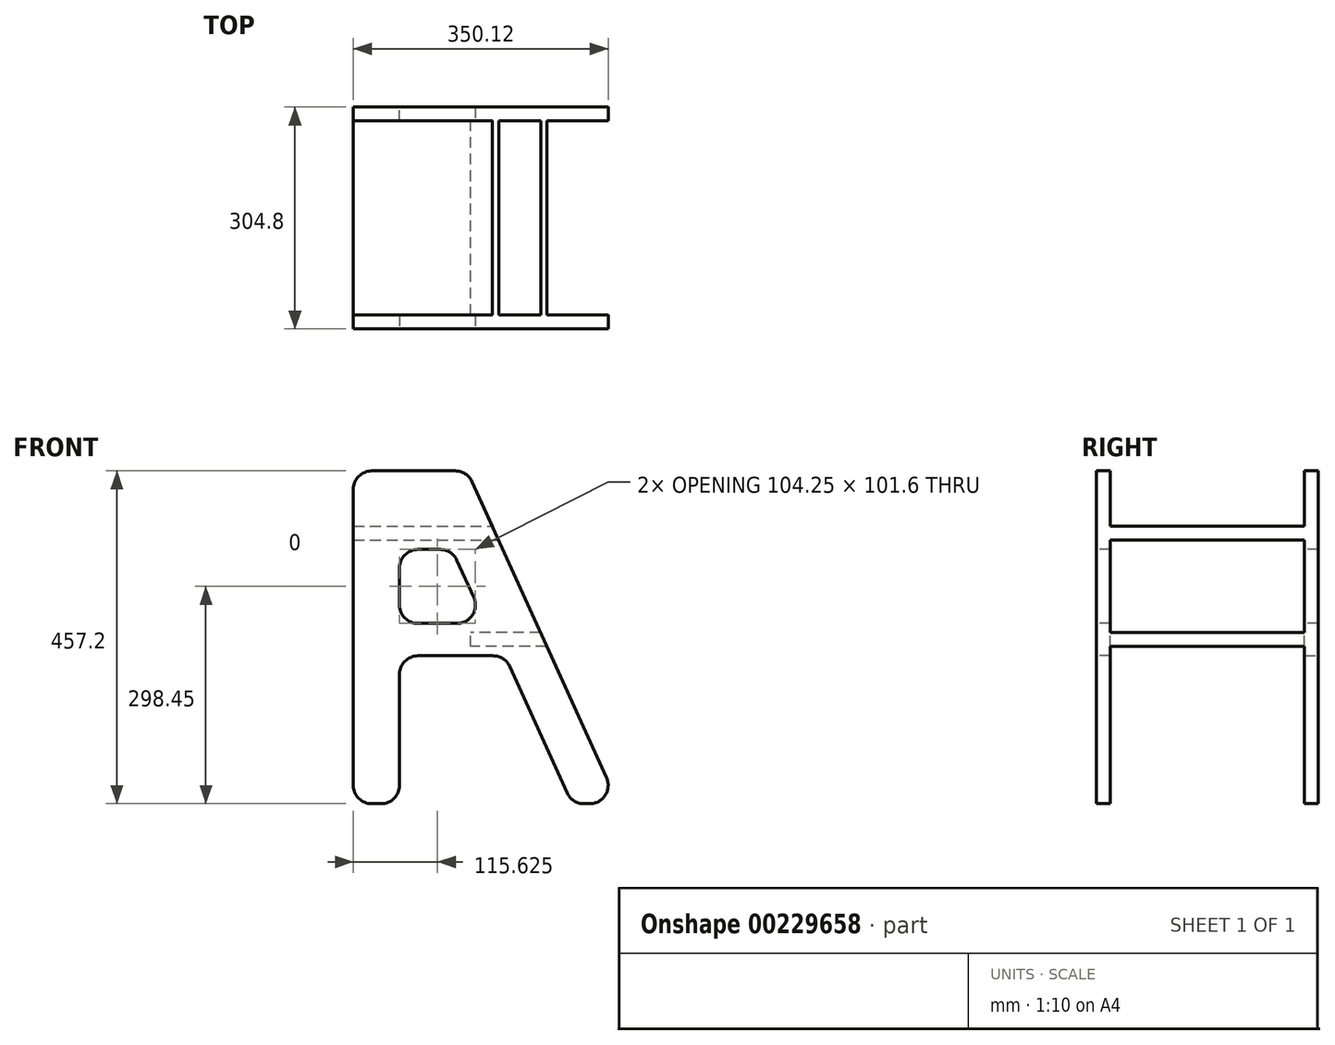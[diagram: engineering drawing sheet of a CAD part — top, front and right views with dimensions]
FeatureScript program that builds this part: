
annotation { "Feature Type Name" : "Feature", "Feature Type Description" : "" }
export const myFeature = defineFeature(function(context is Context, id is Id, definition is map)
    precondition{}
    {
        {
            var Q0;
            Q0=qCreatedBy(makeId("Front.planeOp"),FACE);
            var sketch = newSketch(context, id + "F0", { "sketchPlane" : qUnion([Q0])});
            skLineSegment(sketch, "E0", {"start": v(156.34, 0) * mm, "end": v(153.47, 0) * mm});
            skLineSegment(sketch, "E1", {"start": v(-140.3, 0) * mm, "end": v(-127.6, 0) * mm});
            skLineSegment(sketch, "E2", {"start": v(-165.7, 25.4) * mm, "end": v(-165.7, 304.8) * mm});
            skLineSegment(sketch, "E3", {"start": v(-140.3, 330.2) * mm, "end": v(-25.68, 330.2) * mm});
            skLineSegment(sketch, "E4", {"start": v(-4.4, 318.66) * mm, "end": v(177.62, 39.26) * mm});
            skLineSegment(sketch, "E5", {"start": v(132.19, 11.54) * mm, "end": v(51.03, 136.1) * mm});
            skLineSegment(sketch, "E6", {"start": v(29.75, 147.64) * mm, "end": v(-76.8, 147.64) * mm});
            skLineSegment(sketch, "E7", {"start": v(-102.2, 122.24) * mm, "end": v(-102.2, 25.4) * mm});
            skPoint(sketch, "E8.visualSharp", {"position": v(-165.7, 0) * mm});
            skArc(sketch, "E8.filletArc", {"start": v(-165.7, 25.4) * mm, "mid": v(-158.26, 7.44) * mm, "end": v(-140.3, 0) * mm});
            skPoint(sketch, "E9.visualSharp", {"position": v(-102.2, 0) * mm});
            skArc(sketch, "E9.filletArc", {"start": v(-127.6, 0) * mm, "mid": v(-109.64, 7.44) * mm, "end": v(-102.2, 25.4) * mm});
            skPoint(sketch, "E10.visualSharp", {"position": v(139.7, 0) * mm});
            skArc(sketch, "E10.filletArc", {"start": v(132.19, 11.54) * mm, "mid": v(141.36, 3.07) * mm, "end": v(153.47, 0) * mm});
            skPoint(sketch, "E11.visualSharp", {"position": v(203.2, 0) * mm});
            skArc(sketch, "E11.filletArc", {"start": v(156.34, 0) * mm, "mid": v(178.67, 13.3) * mm, "end": v(177.62, 39.26) * mm});
            skPoint(sketch, "E12.visualSharp", {"position": v(-165.7, 330.2) * mm});
            skArc(sketch, "E12.filletArc", {"start": v(-140.3, 330.2) * mm, "mid": v(-158.26, 322.76) * mm, "end": v(-165.7, 304.8) * mm});
            skPoint(sketch, "E13.visualSharp", {"position": v(-11.91, 330.2) * mm});
            skArc(sketch, "E13.filletArc", {"start": v(-4.4, 318.66) * mm, "mid": v(-13.57, 327.13) * mm, "end": v(-25.68, 330.2) * mm});
            skPoint(sketch, "E14.visualSharp", {"position": v(-102.2, 147.64) * mm});
            skArc(sketch, "E14.filletArc", {"start": v(-76.8, 147.64) * mm, "mid": v(-94.76, 140.2) * mm, "end": v(-102.2, 122.24) * mm});
            skPoint(sketch, "E15.visualSharp", {"position": v(43.52, 147.64) * mm});
            skArc(sketch, "E15.filletArc", {"start": v(51.03, 136.1) * mm, "mid": v(41.85, 144.57) * mm, "end": v(29.75, 147.64) * mm});
            skSolve(sketch);
        }
        {
            var Q0;
            Q0=qCreatedBy(makeId("Front.planeOp"),FACE);
            cPlane(context, id + "F1", {"entities" : qUnion([Q0]), "cplaneType" : CPlaneType.OFFSET, "offset" : 152.4 * mm, "width" : 152.4 * mm, "height" : 152.4 * mm});
        }
        {
            var Q0;
            Q0=qCreatedBy(id+"F1.planeOp",FACE);
            cPlane(context, id + "F2", {"entities" : qUnion([Q0]), "cplaneType" : CPlaneType.OFFSET, "offset" : 304.8 * mm, "oppositeDirection" : true, "width" : 152.4 * mm, "height" : 152.4 * mm});
        }
        {
            var Q0;
            Q0=qCreatedBy(id+"F2.planeOp",FACE);
            var sketch = newSketch(context, id + "F3", { "sketchPlane" : qUnion([Q0])});
            skLineSegment(sketch, "E16", {"start": v(163.76, 0) * mm, "end": v(156.06, 0) * mm});
            skLineSegment(sketch, "E17", {"start": v(-135.56, 0) * mm, "end": v(-122.86, 0) * mm});
            skLineSegment(sketch, "E18", {"start": v(-160.96, 25.4) * mm, "end": v(-160.96, 431.8) * mm});
            skLineSegment(sketch, "E19", {"start": v(-135.56, 457.2) * mm, "end": v(-20.94, 457.2) * mm});
            skLineSegment(sketch, "E20", {"start": v(2.19, 442.3) * mm, "end": v(186.88, 35.9) * mm});
            skLineSegment(sketch, "E21", {"start": v(132.93, 14.9) * mm, "end": v(54.12, 188.3) * mm});
            skLineSegment(sketch, "E22", {"start": v(31, 203.2) * mm, "end": v(-72.06, 203.2) * mm});
            skLineSegment(sketch, "E23", {"start": v(-97.46, 177.8) * mm, "end": v(-97.46, 25.4) * mm});
            skPoint(sketch, "E24.visualSharp", {"position": v(-160.96, 0) * mm});
            skArc(sketch, "E24.filletArc", {"start": v(-160.96, 25.4) * mm, "mid": v(-153.52, 7.44) * mm, "end": v(-135.56, 0) * mm});
            skPoint(sketch, "E25.visualSharp", {"position": v(-97.46, 0) * mm});
            skArc(sketch, "E25.filletArc", {"start": v(-122.86, 0) * mm, "mid": v(-104.9, 7.44) * mm, "end": v(-97.46, 25.4) * mm});
            skPoint(sketch, "E26.visualSharp", {"position": v(139.7, 0) * mm});
            skArc(sketch, "E26.filletArc", {"start": v(132.93, 14.9) * mm, "mid": v(142.3, 4.04) * mm, "end": v(156.06, 0) * mm});
            skPoint(sketch, "E27.visualSharp", {"position": v(203.2, 0) * mm});
            skArc(sketch, "E27.filletArc", {"start": v(163.76, 0) * mm, "mid": v(185.11, 11.65) * mm, "end": v(186.88, 35.9) * mm});
            skPoint(sketch, "E28.visualSharp", {"position": v(-160.96, 457.2) * mm});
            skArc(sketch, "E28.filletArc", {"start": v(-135.56, 457.2) * mm, "mid": v(-153.52, 449.76) * mm, "end": v(-160.96, 431.8) * mm});
            skPoint(sketch, "E29.visualSharp", {"position": v(-4.58, 457.2) * mm});
            skArc(sketch, "E29.filletArc", {"start": v(2.19, 442.3) * mm, "mid": v(-7.19, 453.16) * mm, "end": v(-20.94, 457.2) * mm});
            skPoint(sketch, "E30.visualSharp", {"position": v(-97.46, 203.2) * mm});
            skArc(sketch, "E30.filletArc", {"start": v(-72.06, 203.2) * mm, "mid": v(-90.02, 195.76) * mm, "end": v(-97.46, 177.8) * mm});
            skPoint(sketch, "E31.visualSharp", {"position": v(47.35, 203.2) * mm});
            skArc(sketch, "E31.filletArc", {"start": v(54.12, 188.3) * mm, "mid": v(44.75, 199.16) * mm, "end": v(31, 203.2) * mm});
            skSolve(sketch);
        }
        {
            var Q0;
            Q0=qCreatedBy(id+"F1.planeOp",FACE);
            var sketch = newSketch(context, id + "F4", { "sketchPlane" : qUnion([Q0])});
            skLineSegment(sketch, "E32", {"start": v(163.76, 0) * mm, "end": v(156.06, 0) * mm});
            skLineSegment(sketch, "E33", {"start": v(-135.56, 0) * mm, "end": v(-122.86, 0) * mm});
            skLineSegment(sketch, "E34", {"start": v(-160.96, 25.4) * mm, "end": v(-160.96, 431.8) * mm});
            skLineSegment(sketch, "E35", {"start": v(-135.56, 457.2) * mm, "end": v(-20.94, 457.2) * mm});
            skLineSegment(sketch, "E36", {"start": v(2.19, 442.3) * mm, "end": v(186.88, 35.9) * mm});
            skLineSegment(sketch, "E37", {"start": v(132.93, 14.9) * mm, "end": v(54.12, 188.3) * mm});
            skLineSegment(sketch, "E38", {"start": v(31, 203.2) * mm, "end": v(-72.06, 203.2) * mm});
            skLineSegment(sketch, "E39", {"start": v(-97.46, 177.8) * mm, "end": v(-97.46, 25.4) * mm});
            skPoint(sketch, "E40.visualSharp", {"position": v(-160.96, 0) * mm});
            skArc(sketch, "E40.filletArc", {"start": v(-160.96, 25.4) * mm, "mid": v(-153.52, 7.44) * mm, "end": v(-135.56, 0) * mm});
            skPoint(sketch, "E41.visualSharp", {"position": v(-97.46, 0) * mm});
            skArc(sketch, "E41.filletArc", {"start": v(-122.86, 0) * mm, "mid": v(-104.9, 7.44) * mm, "end": v(-97.46, 25.4) * mm});
            skPoint(sketch, "E42.visualSharp", {"position": v(139.7, 0) * mm});
            skArc(sketch, "E42.filletArc", {"start": v(132.93, 14.9) * mm, "mid": v(142.3, 4.04) * mm, "end": v(156.06, 0) * mm});
            skPoint(sketch, "E43.visualSharp", {"position": v(203.2, 0) * mm});
            skArc(sketch, "E43.filletArc", {"start": v(163.76, 0) * mm, "mid": v(185.11, 11.65) * mm, "end": v(186.88, 35.9) * mm});
            skPoint(sketch, "E44.visualSharp", {"position": v(-160.96, 457.2) * mm});
            skArc(sketch, "E44.filletArc", {"start": v(-135.56, 457.2) * mm, "mid": v(-153.52, 449.76) * mm, "end": v(-160.96, 431.8) * mm});
            skPoint(sketch, "E45.visualSharp", {"position": v(-4.58, 457.2) * mm});
            skArc(sketch, "E45.filletArc", {"start": v(2.19, 442.3) * mm, "mid": v(-7.19, 453.16) * mm, "end": v(-20.94, 457.2) * mm});
            skPoint(sketch, "E46.visualSharp", {"position": v(-97.46, 203.2) * mm});
            skArc(sketch, "E46.filletArc", {"start": v(-72.06, 203.2) * mm, "mid": v(-90.02, 195.76) * mm, "end": v(-97.46, 177.8) * mm});
            skPoint(sketch, "E47.visualSharp", {"position": v(47.35, 203.2) * mm});
            skArc(sketch, "E47.filletArc", {"start": v(54.12, 188.3) * mm, "mid": v(44.75, 199.16) * mm, "end": v(31, 203.2) * mm});
            skSolve(sketch);
        }
        {
            var Q0;
            Q0=makeQuery(id+"F4.imprint","IMPRINT",FACE,{"disambiguationData":[TD([[makeQuery(id+"F4.imprint","IMPRINT",EDGE,{"derivedFrom":sQuery(id+"F4.wireOp",EDGE,"E32")}),-1.0]])]});
            extrude(context, id + "F5", {"entities" : qUnion([Q0]), "oppositeDirection" : true, "depth" : 19.05 * mm});
        }
        {
            var Q0;
            Q0=makeQuery(id+"F3.imprint","IMPRINT",FACE,{"disambiguationData":[TD([[makeQuery(id+"F3.imprint","IMPRINT",EDGE,{"derivedFrom":sQuery(id+"F3.wireOp",EDGE,"E16")}),-1.0]])]});
            extrude(context, id + "F6", {"entities" : qUnion([Q0]), "depth" : 19.05 * mm});
        }
        {
            var Q0;
            Q0=qCreatedBy(makeId("Right.planeOp"),FACE);
            var sketch = newSketch(context, id + "F7", { "sketchPlane" : qUnion([Q0])});
            skLineSegment(sketch, "E48.bottom", {"start": v(-139.7, 234.95) * mm, "end": v(139.7, 234.95) * mm});
            skLineSegment(sketch, "E48.top", {"start": v(-139.7, 215.9) * mm, "end": v(139.7, 215.9) * mm});
            skLineSegment(sketch, "E48.left", {"start": v(-139.7, 234.95) * mm, "end": v(-139.7, 215.9) * mm});
            skLineSegment(sketch, "E48.right", {"start": v(139.7, 234.95) * mm, "end": v(139.7, 215.9) * mm});
            skSolve(sketch);
        }
        {
            var Q0;
            Q0=makeQuery(id+"F7.imprint","IMPRINT",FACE,{"disambiguationData":[TD([[makeQuery(id+"F7.imprint","IMPRINT",EDGE,{"derivedFrom":sQuery(id+"F7.wireOp",EDGE,"E48.bottom")}),-1.0]])]});
            extrude(context, id + "F8", {"entities" : qUnion([Q0]), "operationType" : NewBodyOperationType.ADD, "depth" : 112.78 * mm});
        }
        {
            var Q0;
            Q0=makeQuery(id+"F6.opExtrude","SWEPT_FACE",FACE,{"disambiguationData":[OSD([sQuery(id+"F3.wireOp",EDGE,"E18")])]});
            var sketch = newSketch(context, id + "F9", { "sketchPlane" : qUnion([Q0])});
            skLineSegment(sketch, "E49.bottom", {"start": v(-139.7, 381) * mm, "end": v(139.7, 381) * mm});
            skLineSegment(sketch, "E49.top", {"start": v(-139.7, 361.95) * mm, "end": v(139.7, 361.95) * mm});
            skLineSegment(sketch, "E49.left", {"start": v(-139.7, 381) * mm, "end": v(-139.7, 361.95) * mm});
            skLineSegment(sketch, "E49.right", {"start": v(139.7, 381) * mm, "end": v(139.7, 361.95) * mm});
            skSolve(sketch);
        }
        {
            var Q0;
            Q0 = qSketchRegion(id + "F9", true);
            extrude(context, id + "F10", {"entities" : qUnion([Q0]), "operationType" : NewBodyOperationType.ADD, "oppositeDirection" : true, "depth" : 209.8 * mm});
        }
        {
            var Q0;
            Q0=makeQuery(id+"F6.opExtrude","CAP_FACE",FACE,{"disambiguationData":[OSD([sQuery(id+"F3.wireOp",EDGE,"E16"),sQuery(id+"F3.wireOp",EDGE,"E17"),sQuery(id+"F3.wireOp",EDGE,"E18"),sQuery(id+"F3.wireOp",EDGE,"E19"),sQuery(id+"F3.wireOp",EDGE,"E20"),sQuery(id+"F3.wireOp",EDGE,"E21"),sQuery(id+"F3.wireOp",EDGE,"E22"),sQuery(id+"F3.wireOp",EDGE,"E23"),sQuery(id+"F3.wireOp",EDGE,"E24.filletArc"),sQuery(id+"F3.wireOp",EDGE,"E25.filletArc"),sQuery(id+"F3.wireOp",EDGE,"E26.filletArc"),sQuery(id+"F3.wireOp",EDGE,"E27.filletArc"),sQuery(id+"F3.wireOp",EDGE,"E28.filletArc"),sQuery(id+"F3.wireOp",EDGE,"E29.filletArc"),sQuery(id+"F3.wireOp",EDGE,"E30.filletArc"),sQuery(id+"F3.wireOp",EDGE,"E31.filletArc")])],"isStart":true});
            var sketch = newSketch(context, id + "F11", { "sketchPlane" : qUnion([Q0])});
            skLineSegment(sketch, "E50", {"start": v(-14.78, 414.6) * mm, "end": v(-117.13, 189.38) * mm});
            skLineSegment(sketch, "E51", {"start": v(-117.13, 189.38) * mm, "end": v(-147.45, 203.16) * mm});
            skLineSegment(sketch, "E52", {"start": v(-147.45, 203.16) * mm, "end": v(-39.66, 420.54) * mm});
            skLineSegment(sketch, "E53", {"start": v(-14.78, 414.6) * mm, "end": v(-39.66, 420.54) * mm});
            skSolve(sketch);
        }
        {
            var Q0;
            Q0 = qSketchRegion(id + "F11", true);
            extrude(context, id + "F12", {"entities" : qUnion([Q0]), "operationType" : NewBodyOperationType.REMOVE, "oppositeDirection" : true, "depth" : 375.92 * mm});
        }
        {
            var Q0;
            Q0=makeQuery(id+"F5.opExtrude","CAP_FACE",FACE,{"disambiguationData":[OSD([sQuery(id+"F4.wireOp",EDGE,"E32"),sQuery(id+"F4.wireOp",EDGE,"E33"),sQuery(id+"F4.wireOp",EDGE,"E34"),sQuery(id+"F4.wireOp",EDGE,"E35"),sQuery(id+"F4.wireOp",EDGE,"E36"),sQuery(id+"F4.wireOp",EDGE,"E37"),sQuery(id+"F4.wireOp",EDGE,"E38"),sQuery(id+"F4.wireOp",EDGE,"E39"),sQuery(id+"F4.wireOp",EDGE,"E40.filletArc"),sQuery(id+"F4.wireOp",EDGE,"E41.filletArc"),sQuery(id+"F4.wireOp",EDGE,"E42.filletArc"),sQuery(id+"F4.wireOp",EDGE,"E43.filletArc"),sQuery(id+"F4.wireOp",EDGE,"E44.filletArc"),sQuery(id+"F4.wireOp",EDGE,"E45.filletArc"),sQuery(id+"F4.wireOp",EDGE,"E46.filletArc"),sQuery(id+"F4.wireOp",EDGE,"E47.filletArc")])],"isStart":true});
            var sketch = newSketch(context, id + "F13", { "sketchPlane" : qUnion([Q0])});
            skLineSegment(sketch, "E54.bottom", {"start": v(-22.1, 406.4) * mm, "end": v(-122.86, 406.4) * mm});
            skLineSegment(sketch, "E54.top", {"start": v(-22.1, 431.8) * mm, "end": v(-122.86, 431.8) * mm});
            skLineSegment(sketch, "E54.left", {"start": v(-9.4, 419.1) * mm, "end": v(-9.4, 419.1) * mm});
            skLineSegment(sketch, "E54.right", {"start": v(-135.56, 419.1) * mm, "end": v(-135.56, 419.1) * mm});
            skPoint(sketch, "E54.middle", {"position": v(-72.48, 419.1) * mm});
            skPoint(sketch, "E55.visualSharp", {"position": v(-9.4, 431.8) * mm});
            skArc(sketch, "E55.filletArc", {"start": v(-9.4, 419.1) * mm, "mid": v(-13.12, 428.08) * mm, "end": v(-22.1, 431.8) * mm});
            skPoint(sketch, "E56.visualSharp", {"position": v(-9.4, 406.4) * mm});
            skArc(sketch, "E56.filletArc", {"start": v(-22.1, 406.4) * mm, "mid": v(-13.12, 410.12) * mm, "end": v(-9.4, 419.1) * mm});
            skPoint(sketch, "E57.visualSharp", {"position": v(-135.56, 431.8) * mm});
            skArc(sketch, "E57.filletArc", {"start": v(-122.86, 431.8) * mm, "mid": v(-131.84, 428.08) * mm, "end": v(-135.56, 419.1) * mm});
            skPoint(sketch, "E58.visualSharp", {"position": v(-135.56, 406.4) * mm});
            skArc(sketch, "E58.filletArc", {"start": v(-135.56, 419.1) * mm, "mid": v(-131.84, 410.12) * mm, "end": v(-122.86, 406.4) * mm});
            skLineSegment(sketch, "E59", {"start": v(-9.4, 431.8) * mm, "end": v(-9.4, 406.4) * mm});
            skSolve(sketch);
        }
        {
            var Q0;
            Q0=makeQuery(id+"F5.opExtrude","CAP_FACE",FACE,{"disambiguationData":[OSD([sQuery(id+"F4.wireOp",EDGE,"E32"),sQuery(id+"F4.wireOp",EDGE,"E33"),sQuery(id+"F4.wireOp",EDGE,"E34"),sQuery(id+"F4.wireOp",EDGE,"E35"),sQuery(id+"F4.wireOp",EDGE,"E36"),sQuery(id+"F4.wireOp",EDGE,"E37"),sQuery(id+"F4.wireOp",EDGE,"E38"),sQuery(id+"F4.wireOp",EDGE,"E39"),sQuery(id+"F4.wireOp",EDGE,"E40.filletArc"),sQuery(id+"F4.wireOp",EDGE,"E41.filletArc"),sQuery(id+"F4.wireOp",EDGE,"E42.filletArc"),sQuery(id+"F4.wireOp",EDGE,"E43.filletArc"),sQuery(id+"F4.wireOp",EDGE,"E44.filletArc"),sQuery(id+"F4.wireOp",EDGE,"E45.filletArc"),sQuery(id+"F4.wireOp",EDGE,"E46.filletArc"),sQuery(id+"F4.wireOp",EDGE,"E47.filletArc")])],"isStart":true});
            var sketch = newSketch(context, id + "F14", { "sketchPlane" : qUnion([Q0])});
            skLineSegment(sketch, "E60", {"start": v(4.58, 283.56) * mm, "end": v(-18.5, 334.36) * mm});
            skLineSegment(sketch, "E61", {"start": v(-41.63, 349.25) * mm, "end": v(-72.06, 349.25) * mm});
            skLineSegment(sketch, "E62", {"start": v(-97.46, 323.85) * mm, "end": v(-97.46, 273.05) * mm});
            skLineSegment(sketch, "E63", {"start": v(-72.06, 247.65) * mm, "end": v(-18.54, 247.65) * mm});
            skPoint(sketch, "E64.visualSharp", {"position": v(-97.46, 349.25) * mm});
            skArc(sketch, "E64.filletArc", {"start": v(-72.06, 349.25) * mm, "mid": v(-90.02, 341.81) * mm, "end": v(-97.46, 323.85) * mm});
            skPoint(sketch, "E65.visualSharp", {"position": v(-25.27, 349.25) * mm});
            skArc(sketch, "E65.filletArc", {"start": v(-18.5, 334.36) * mm, "mid": v(-27.88, 345.2) * mm, "end": v(-41.63, 349.25) * mm});
            skPoint(sketch, "E66.visualSharp", {"position": v(20.9, 247.65) * mm});
            skArc(sketch, "E66.filletArc", {"start": v(-18.54, 247.65) * mm, "mid": v(2.81, 259.3) * mm, "end": v(4.58, 283.56) * mm});
            skPoint(sketch, "E67.visualSharp", {"position": v(-97.46, 247.65) * mm});
            skArc(sketch, "E67.filletArc", {"start": v(-97.46, 273.05) * mm, "mid": v(-90.02, 255.09) * mm, "end": v(-72.06, 247.65) * mm});
            skSolve(sketch);
        }
        {
            var Q0;
            Q0 = qSketchRegion(id + "F14", true);
            extrude(context, id + "F15", {"entities" : qUnion([Q0]), "operationType" : NewBodyOperationType.REMOVE, "oppositeDirection" : true, "depth" : 313.44 * mm});
        }
    });
